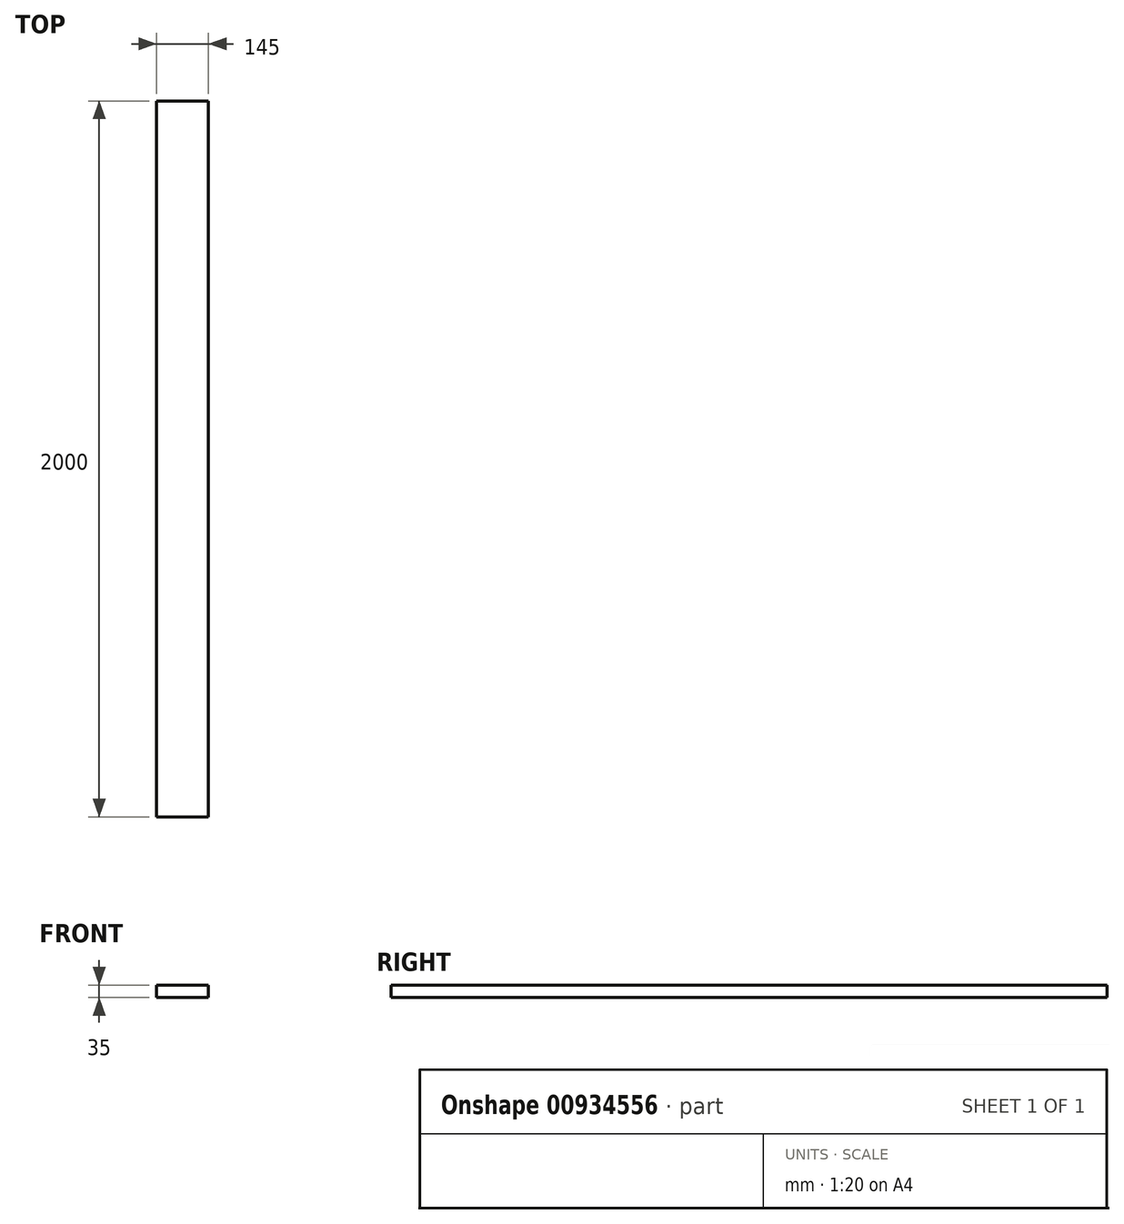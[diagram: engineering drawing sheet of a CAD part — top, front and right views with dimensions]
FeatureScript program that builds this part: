
annotation { "Feature Type Name" : "Feature", "Feature Type Description" : "" }
export const myFeature = defineFeature(function(context is Context, id is Id, definition is map)
    precondition{}
    {
        {
            var Q0;
            Q0=qCreatedBy(makeId("Front.planeOp"),FACE);
            var sketch = newSketch(context, id + "F0", { "sketchPlane" : qUnion([Q0])});
            skLineSegment(sketch, "E0.bottom", {"start": v(72.5, 17.5) * mm, "end": v(-72.5, 17.5) * mm});
            skLineSegment(sketch, "E0.top", {"start": v(72.5, -17.5) * mm, "end": v(-72.5, -17.5) * mm});
            skLineSegment(sketch, "E0.left", {"start": v(72.5, 17.5) * mm, "end": v(72.5, -17.5) * mm});
            skLineSegment(sketch, "E0.right", {"start": v(-72.5, 17.5) * mm, "end": v(-72.5, -17.5) * mm});
            skPoint(sketch, "E0.middle", {"position": v(0, 0) * mm});
            skSolve(sketch);
        }
        {
            var Q0;
            Q0=makeQuery(id+"F0.imprint","IMPRINT",FACE,{"disambiguationData":[TD([[makeQuery(id+"F0.imprint","IMPRINT",EDGE,{"derivedFrom":sQuery(id+"F0.wireOp",EDGE,"E0.bottom")}),1.0]])]});
            extrude(context, id + "F1", {"entities" : qUnion([Q0]), "endBound" : BoundingType.SYMMETRIC, "depth" : 2000 * mm, "offsetDistance" : 25 * mm});
        }
    });
